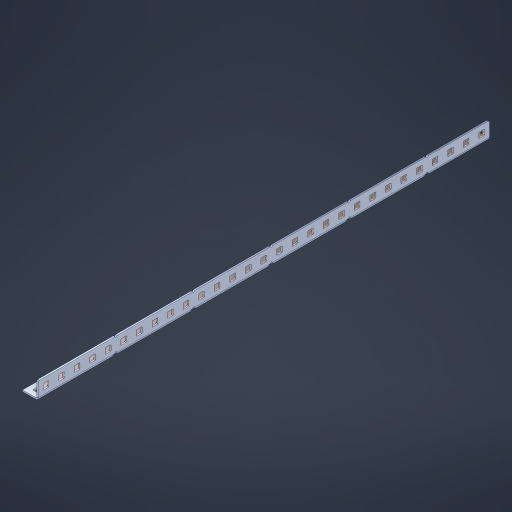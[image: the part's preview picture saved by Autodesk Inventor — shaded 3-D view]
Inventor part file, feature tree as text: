
AUTODESK INVENTOR PART (.ipt)
format: ipt  version: 2023 (Build 270158000, 158)  size: 928,768 bytes
history: native  units: in
note: dims shown in document units (in); Inventor stores cm internally (conversion verified against a paired STEP export)
features: other x63, extrude x57, sheet_metal_op x10, sketch x8, mirror x1, pattern_linear x1, chamfer x1
ambient origin geometry x8: Origin, YZ Plane, XZ Plane, XY Plane, X Axis, Y Axis, Z Axis, Center Point
bodies: Solid1 (feature_tree), Body (feature_tree)
feature tree (141):
  other  "Flange Pattern Plane"
  sheet_metal_op  "Flange Pattern"
  sheet_metal_op  "Body Pattern"
  other  "Arc Length"
  mirror  "Notch Mirror"
  pattern_linear  "Notch Pattern"  Spacing1=0.1875in  [1 undecoded]
  chamfer  "End Chamfer"
  extrude  "Half Cut"  Depth=0.0469in
  sketch  "Sketch1"  dims[d0=2.5in]
  other  "Plate1"
  sketch  "Sketch2"  dims[d1=14.5in]
  other  "Plate2"
  sheet_metal_op  "Bend1"
  sheet_metal_op  "Corner1"
  sketch  "Sketch3"  dims[d2=0.0469in]
  other  "Flange Pattern Sketch"
  sketch  "Sketch7"  dims[d3=0.0469in]
  other  "Srf1"
  other  "Srf2"
  sketch  "Sketch8"  dims[d4=0.0234in]
  sketch  "Sketch9"  dims[d5=0.0938in]
  other  "Srf91"
  sheet_metal_op  "Body Pattern Sketch"
  other  "Srf92"
  sketch  "Sketch13"  dims[d6=0.0469in]
  sketch  "Sketch14"  dims[d7=0.5in d8=90.0deg d9=0.0312in d10=0.1875in d11=0.0469in d12=0.0469in d16=0.182in d17=0.02in d18=0.0469in d19=0.0in d20=0.25in d21=0.25in d46=0.172in d47=1.0in d48=0.0in d49=0.182in d50=0.02in d51=0.25in d52=0.25in d53=0.0469in d54=0.0in d55=0.172in d56=1.0in d57=0.0in d60=11.4173in d62=0.5in d63=0.3937in d65=0.5in d85=0.1227in d86=0.1659in d88=0.04in d89=0.0469in d90=0.0in d91=0.04in d92=0.0491in d95=2.5in d96=0.04in d97=0.25in d98=45.0deg d101=0.0in d102=2.497in d131=0.5in d132=11.4173in d134=0.5in d139=0.5in]
  other  "Srf856"
  other  "Srf1310"
  other  "Srf1311"
  other  "Srf1312"
  other  "Srf1376"
  other  "Srf1377"
  other  "Srf1728"
  other  "Srf1755"
  other  "Srf1878"
  other  "Srf1879"
  other  "Srf1880"
  other  "Srf1881"
  other  "Srf1882"
  other  "Srf1883"
  other  "Srf1884"
  other  "Srf1885"
  other  "Srf1886"
  other  "Srf1887"
  other  "Srf1888"
  other  "Srf1889"
  other  "Srf1890"
  other  "Srf1891"
  other  "Srf1892"
  other  "Srf1893"
  other  "Srf1894"
  other  "Srf1895"
  other  "Srf1896"
  other  "Srf1897"
  other  "Srf1898"
  other  "Srf1899"
  other  "Srf1900"
  other  "Srf1942"
  other  "Srf1943"
  other  "Srf1944"
  other  "Srf1945"
  other  "Srf1946"
  other  "Srf1947"
  other  "Srf1948"
  other  "Srf1949"
  other  "Srf1950"
  other  "Srf1951"
  other  "Srf1952"
  other  "Srf1953"
  other  "Srf1954"
  other  "Srf1955"
  other  "Srf1956"
  other  "Srf1957"
  other  "Srf1958"
  other  "Srf1959"
  other  "Srf1960"
  other  "Srf1961"
  other  "Srf1962"
  other  "Srf1963"
  other  "Srf1964"
  sheet_metal_op  "Flange Stamp"
  sheet_metal_op  "Flange Circle"
  sheet_metal_op  "Body Stamp"
  sheet_metal_op  "Body Circle"
  sheet_metal_op  "Notch"
  extrude  "ExtrusionSrf2"  Depth=0.0469in
  extrude  "ExtrusionSrf92"  Depth=0.5in
  extrude  "ExtrusionSrf856"  Depth=0.02in
  extrude  "ExtrusionSrf1310"  Depth=0.0469in
  extrude  "ExtrusionSrf1311"  TaperAngle=0.0deg  [1 undecoded]
  extrude  "ExtrusionSrf1312"  Depth=0.5in
  extrude  "ExtrusionSrf1376"  Depth=0.5in
  extrude  "ExtrusionSrf1377"  Depth=0.5in
  extrude  "ExtrusionSrf1728"  Depth=0.5in TaperAngle=0.0deg
  extrude  "ExtrusionSrf1755"  Depth=0.5in
  extrude  "ExtrusionSrf1878"  Depth=0.02in
  extrude  "ExtrusionSrf1879"  Depth=0.5in
  extrude  "ExtrusionSrf1880"  Depth=0.5in
  extrude  "ExtrusionSrf1881"  Depth=0.0469in
  extrude  "ExtrusionSrf1882"  TaperAngle=0.0deg  [1 undecoded]
  extrude  "ExtrusionSrf1883"  Depth=0.5in
  extrude  "ExtrusionSrf1884"  Depth=0.5in TaperAngle=0.0deg
  extrude  "ExtrusionSrf1885"  Depth=0.5in
  extrude  "ExtrusionSrf1886"  Depth=0.5in
  extrude  "ExtrusionSrf1887"  Depth=0.5in
  extrude  "ExtrusionSrf1888"  Depth=0.5in
  extrude  "ExtrusionSrf1889"  Depth=0.5in
  extrude  "ExtrusionSrf1890"  Depth=0.0469in
  extrude  "ExtrusionSrf1891"  TaperAngle=0.0deg  [1 undecoded]
  extrude  "ExtrusionSrf1892"  Depth=0.5in
  extrude  "ExtrusionSrf1893"  Depth=0.5in
  extrude  "ExtrusionSrf1894"  Depth=0.5in
  extrude  "ExtrusionSrf1895"  Depth=0.5in TaperAngle=45.0deg
  extrude  "ExtrusionSrf1896"  TaperAngle=0.0deg  [1 undecoded]
  extrude  "ExtrusionSrf1897"  Depth=0.5in
  extrude  "ExtrusionSrf1898"  Depth=0.5in
  extrude  "ExtrusionSrf1899"  Depth=0.5in
  extrude  "ExtrusionSrf1900"  Depth=0.5in
  extrude  "ExtrusionSrf1942"  Depth=0.5in
  extrude  "ExtrusionSrf1943"  [1 undecoded]
  extrude  "ExtrusionSrf1944"  [1 undecoded]
  extrude  "ExtrusionSrf1945"  [1 undecoded]
  extrude  "ExtrusionSrf1946"  [1 undecoded]
  extrude  "ExtrusionSrf1947"  [1 undecoded]
  extrude  "ExtrusionSrf1948"  [1 undecoded]
  extrude  "ExtrusionSrf1949"  [1 undecoded]
  extrude  "ExtrusionSrf1950"  [1 undecoded]
  extrude  "ExtrusionSrf1951"  [1 undecoded]
  extrude  "ExtrusionSrf1952"  [1 undecoded]
  extrude  "ExtrusionSrf1953"  [1 undecoded]
  extrude  "ExtrusionSrf1954"  [1 undecoded]
  extrude  "ExtrusionSrf1955"  [1 undecoded]
  extrude  "ExtrusionSrf1956"  [1 undecoded]
  extrude  "ExtrusionSrf1957"  [1 undecoded]
  extrude  "ExtrusionSrf1958"  [1 undecoded]
  extrude  "ExtrusionSrf1959"  [1 undecoded]
  extrude  "ExtrusionSrf1960"  [1 undecoded]
  extrude  "ExtrusionSrf1961"  [1 undecoded]
  extrude  "ExtrusionSrf1962"  [1 undecoded]
  extrude  "ExtrusionSrf1963"  [1 undecoded]
  extrude  "ExtrusionSrf1964"  [1 undecoded]
note: 27 required parameter values undecoded (feature->parameter linkage not recoverable at this tier; creation-order binding heuristic only, values carry confidence <= 0.55)
